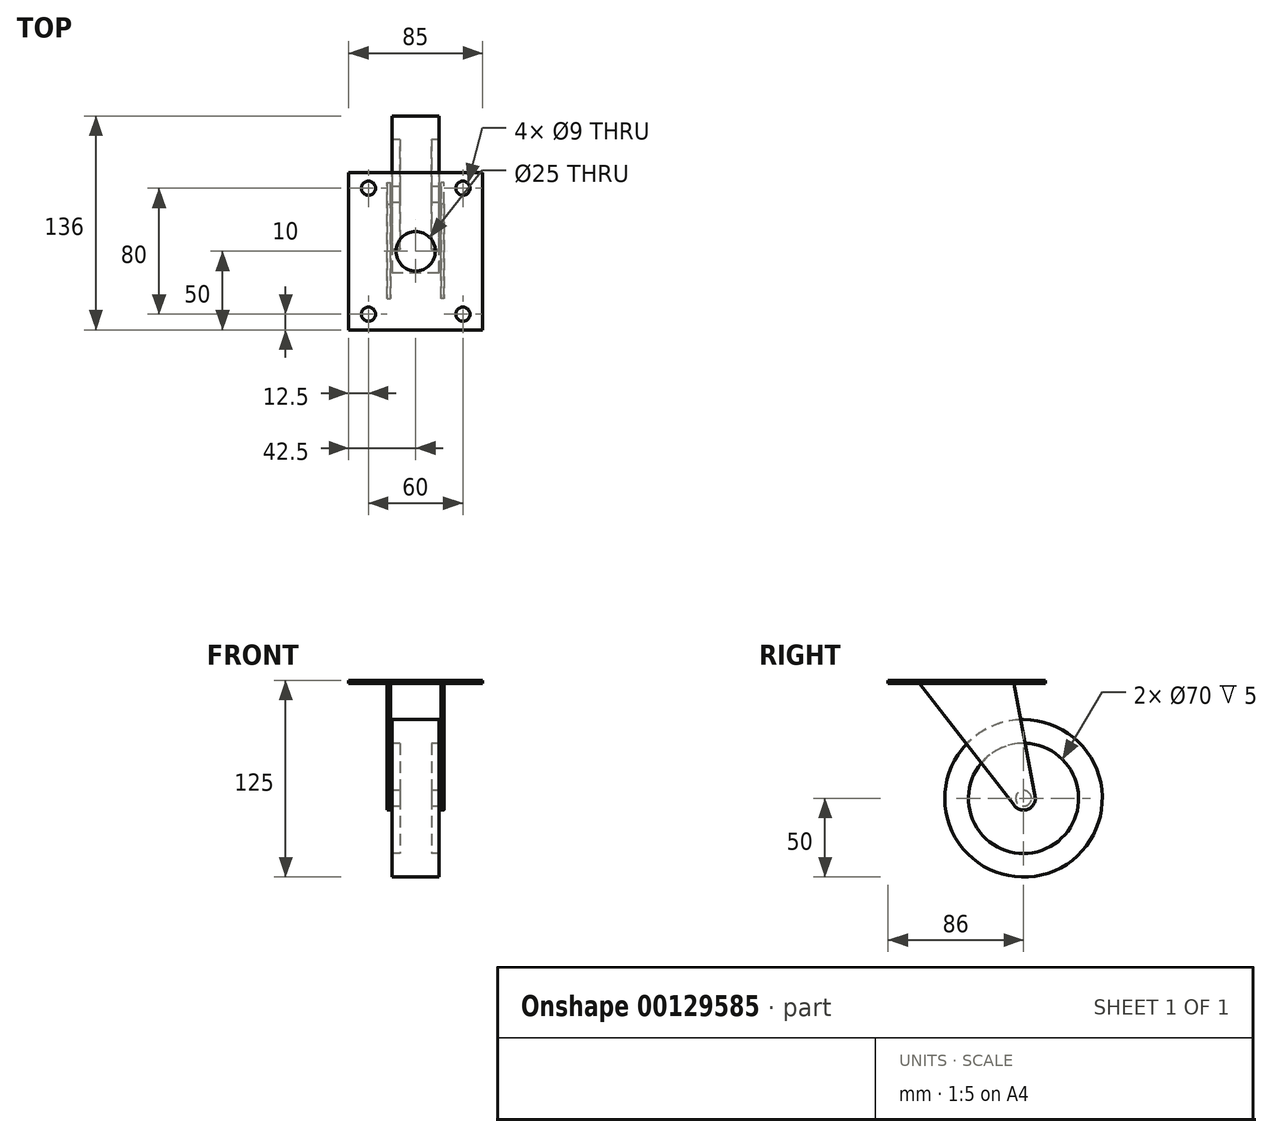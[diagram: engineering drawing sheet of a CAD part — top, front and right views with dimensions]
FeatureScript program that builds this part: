
annotation { "Feature Type Name" : "Feature", "Feature Type Description" : "" }
export const myFeature = defineFeature(function(context is Context, id is Id, definition is map)
    precondition{}
    {
        {
            var Q0;
            Q0=qCreatedBy(makeId("Front.planeOp"),FACE);
            var sketch = newSketch(context, id + "F0", { "sketchPlane" : qUnion([Q0])});
            skLineSegment(sketch, "E0", {"start": v(10, 5) * mm, "end": v(10, 35) * mm});
            skLineSegment(sketch, "E1", {"start": v(10, 35) * mm, "end": v(15, 35) * mm});
            skLineSegment(sketch, "E2", {"start": v(15, 35) * mm, "end": v(15, 50) * mm});
            skLineSegment(sketch, "E3", {"start": v(15, 50) * mm, "end": v(-15, 50) * mm});
            skLineSegment(sketch, "E4", {"start": v(-15, 50) * mm, "end": v(-15, 35) * mm});
            skLineSegment(sketch, "E5", {"start": v(-15, 35) * mm, "end": v(-10, 35) * mm});
            skLineSegment(sketch, "E6", {"start": v(-10, 35) * mm, "end": v(-10, 5) * mm});
            skLineSegment(sketch, "E7", {"start": v(0, 0) * mm, "end": v(0, 50) * mm, "construction": true});
            skLineSegment(sketch, "E8", {"start": v(-10, 5) * mm, "end": v(-16, 5) * mm});
            skLineSegment(sketch, "E9", {"start": v(-16, 5) * mm, "end": v(-16, 0) * mm});
            skLineSegment(sketch, "E10", {"start": v(-16, 0) * mm, "end": v(16, 0) * mm});
            skLineSegment(sketch, "E11", {"start": v(16, 0) * mm, "end": v(16, 5) * mm});
            skLineSegment(sketch, "E12", {"start": v(16, 5) * mm, "end": v(10, 5) * mm});
            skSolve(sketch);
        }
        {
            var Q0;
            Q0 = qSketchRegion(id + "F0", true);
            var Q1;
            Q1=sQuery(id+"F0.wireOp",EDGE,"E10");
            revolve(context, id + "F1", {"entities" : qUnion([Q0]), "axis" : qUnion([Q1]), "revolveType" : RevolveType.FULL});
        }
        {
            var Q0;
            Q0=makeQuery(id+"F1.opRevolve","SWEPT_FACE",FACE,{"disambiguationData":[OSD([sQuery(id+"F0.wireOp",EDGE,"E9")])]});
            var sketch = newSketch(context, id + "F2", { "sketchPlane" : qUnion([Q0])});
            skArc(sketch, "E13", {"start": v(-7.5, 0) * mm, "mid": v(-2.43, -7.1) * mm, "end": v(5.93, -4.6) * mm});
            skLineSegment(sketch, "E14", {"start": v(0, 0) * mm, "end": v(36, 0) * mm, "construction": true});
            skLineSegment(sketch, "E15", {"start": v(36, 0) * mm, "end": v(36, 73) * mm, "construction": true});
            skLineSegment(sketch, "E16", {"start": v(6, 73) * mm, "end": v(66, 73) * mm});
            skLineSegment(sketch, "E17", {"start": v(66, 73) * mm, "end": v(5.93, -4.6) * mm});
            skLineSegment(sketch, "E18", {"start": v(6, 73) * mm, "end": v(-7.5, 0) * mm});
            skSolve(sketch);
        }
        {
            var Q0;
            Q0 = qSketchRegion(id + "F2", true);
            extrude(context, id + "F3", {"entities" : qUnion([Q0]), "operationType" : NewBodyOperationType.ADD, "depth" : 2 * mm});
        }
        {
            var Q0;
            Q0=makeQuery(id+"F1.opRevolve","SWEPT_FACE",FACE,{"disambiguationData":[OSD([sQuery(id+"F0.wireOp",EDGE,"E11")])]});
            var sketch = newSketch(context, id + "F4", { "sketchPlane" : qUnion([Q0])});
            skArc(sketch, "E19.0", {"start": v(7.5, 0) * mm, "mid": v(2.43, -7.1) * mm, "end": v(-5.93, -4.6) * mm});
            skLineSegment(sketch, "E19.3", {"start": v(-6, 73) * mm, "end": v(-66, 73) * mm});
            skLineSegment(sketch, "E19.4", {"start": v(-66, 73) * mm, "end": v(-5.93, -4.6) * mm});
            skLineSegment(sketch, "E19.5", {"start": v(-6, 73) * mm, "end": v(7.5, 0) * mm});
            skSolve(sketch);
        }
        {
            var Q0;
            Q0 = qSketchRegion(id + "F4", true);
            extrude(context, id + "F5", {"entities" : qUnion([Q0]), "operationType" : NewBodyOperationType.ADD, "depth" : 2 * mm});
        }
        {
            var Q0;
            Q0=makeQuery(id+"F3.opExtrude","SWEPT_FACE",FACE,{"disambiguationData":[OSD([sQuery(id+"F2.wireOp",EDGE,"E16")])]});
            var sketch = newSketch(context, id + "F6", { "sketchPlane" : qUnion([Q0])});
            skLineSegment(sketch, "E20", {"start": v(0, 0) * mm, "end": v(0, -36) * mm, "construction": true});
            skLineSegment(sketch, "E21.bottom", {"start": v(-42.5, 14) * mm, "end": v(42.5, 14) * mm});
            skLineSegment(sketch, "E21.top", {"start": v(-42.5, -86) * mm, "end": v(42.5, -86) * mm});
            skLineSegment(sketch, "E21.left", {"start": v(-42.5, 14) * mm, "end": v(-42.5, -86) * mm});
            skLineSegment(sketch, "E21.right", {"start": v(42.5, 14) * mm, "end": v(42.5, -86) * mm});
            skPoint(sketch, "E21.middle", {"position": v(0, -36) * mm});
            skLineSegment(sketch, "E22.bottom", {"start": v(-30, 4) * mm, "end": v(30, 4) * mm, "construction": true});
            skLineSegment(sketch, "E22.top", {"start": v(-30, -76) * mm, "end": v(30, -76) * mm, "construction": true});
            skLineSegment(sketch, "E22.left", {"start": v(-30, 4) * mm, "end": v(-30, -76) * mm, "construction": true});
            skLineSegment(sketch, "E22.right", {"start": v(30, 4) * mm, "end": v(30, -76) * mm, "construction": true});
            skCircle(sketch, "E23", {"center": v(-30, 4) * mm, "radius": 4.5 * mm});
            skCircle(sketch, "E24", {"center": v(30, 4) * mm, "radius": 4.5 * mm});
            skCircle(sketch, "E25", {"center": v(30, -76) * mm, "radius": 4.5 * mm});
            skCircle(sketch, "E26", {"center": v(-30, -76) * mm, "radius": 4.5 * mm});
            skCircle(sketch, "E27", {"center": v(0, -36) * mm, "radius": 12.5 * mm});
            skSolve(sketch);
        }
        {
            var Q0;
            Q0 = qSketchRegion(id + "F6", true);
            extrude(context, id + "F7", {"entities" : qUnion([Q0]), "operationType" : NewBodyOperationType.ADD, "depth" : 2 * mm});
        }
    });
